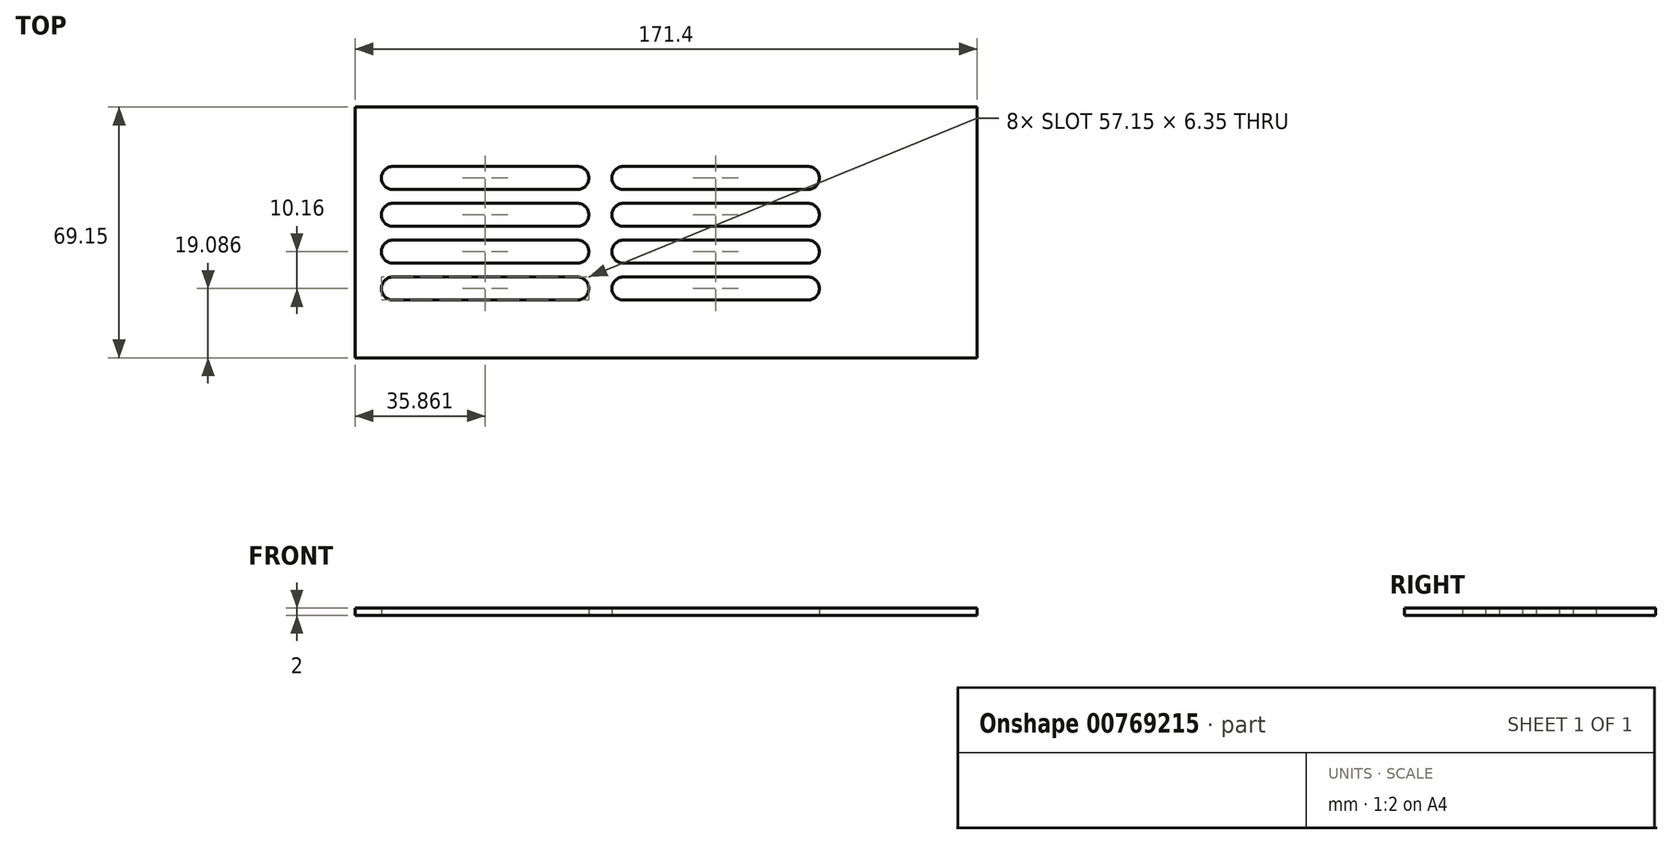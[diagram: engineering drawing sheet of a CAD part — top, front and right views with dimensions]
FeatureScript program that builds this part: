
annotation { "Feature Type Name" : "Feature", "Feature Type Description" : "" }
export const myFeature = defineFeature(function(context is Context, id is Id, definition is map)
    precondition{}
    {
        {
            var Q0;
            Q0=qCreatedBy(makeId("Top.planeOp"),FACE);
            var sketch = newSketch(context, id + "F0", { "sketchPlane" : qUnion([Q0])});
            skLineSegment(sketch, "E0.bottom", {"start": v(-93.16, 23.65) * mm, "end": v(-42.36, 23.65) * mm});
            skLineSegment(sketch, "E0.top", {"start": v(-93.16, 17.3) * mm, "end": v(-42.36, 17.3) * mm});
            skLineSegment(sketch, "E0.left", {"start": v(-96.33, 20.48) * mm, "end": v(-96.33, 20.48) * mm});
            skLineSegment(sketch, "E0.right", {"start": v(-39.18, 20.48) * mm, "end": v(-39.18, 20.48) * mm});
            skPoint(sketch, "E1.visualSharp", {"position": v(-96.33, 23.65) * mm});
            skArc(sketch, "E1.filletArc", {"start": v(-93.16, 23.65) * mm, "mid": v(-95.4, 22.72) * mm, "end": v(-96.33, 20.48) * mm});
            skPoint(sketch, "E2.visualSharp", {"position": v(-96.33, 17.3) * mm});
            skArc(sketch, "E2.filletArc", {"start": v(-96.33, 20.48) * mm, "mid": v(-95.4, 18.23) * mm, "end": v(-93.16, 17.3) * mm});
            skPoint(sketch, "E3.visualSharp", {"position": v(-39.18, 17.3) * mm});
            skArc(sketch, "E3.filletArc", {"start": v(-42.36, 17.3) * mm, "mid": v(-40.11, 18.23) * mm, "end": v(-39.18, 20.48) * mm});
            skPoint(sketch, "E4.visualSharp", {"position": v(-39.18, 23.65) * mm});
            skArc(sketch, "E4.filletArc", {"start": v(-39.18, 20.48) * mm, "mid": v(-40.11, 22.72) * mm, "end": v(-42.36, 23.65) * mm});
            skPoint(sketch, "E5.0.1.0", {"position": v(-39.18, 7.14) * mm});
            skLineSegment(sketch, "E5.0.1.1", {"start": v(-93.16, 7.14) * mm, "end": v(-42.36, 7.14) * mm});
            skPoint(sketch, "E5.0.1.2", {"position": v(-96.33, 13.5) * mm});
            skPoint(sketch, "E5.0.1.3", {"position": v(-39.18, 13.5) * mm});
            skPoint(sketch, "E5.0.1.4", {"position": v(-96.33, 7.14) * mm});
            skLineSegment(sketch, "E5.0.1.5", {"start": v(-93.16, 13.5) * mm, "end": v(-42.36, 13.5) * mm});
            skArc(sketch, "E5.0.1.6", {"start": v(-42.36, 7.14) * mm, "mid": v(-40.11, 8.07) * mm, "end": v(-39.18, 10.32) * mm});
            skArc(sketch, "E5.0.1.7", {"start": v(-96.33, 10.32) * mm, "mid": v(-95.4, 8.07) * mm, "end": v(-93.16, 7.14) * mm});
            skArc(sketch, "E5.0.1.8", {"start": v(-93.16, 13.5) * mm, "mid": v(-95.4, 12.56) * mm, "end": v(-96.33, 10.32) * mm});
            skArc(sketch, "E5.0.1.9", {"start": v(-39.18, 10.32) * mm, "mid": v(-40.11, 12.56) * mm, "end": v(-42.36, 13.5) * mm});
            skLineSegment(sketch, "E5.0.1.10", {"start": v(-96.33, 10.32) * mm, "end": v(-96.33, 10.32) * mm});
            skLineSegment(sketch, "E5.0.1.11", {"start": v(-39.18, 10.32) * mm, "end": v(-39.18, 10.32) * mm});
            skPoint(sketch, "E5.0.2.0", {"position": v(-39.18, -3.02) * mm});
            skLineSegment(sketch, "E5.0.2.1", {"start": v(-93.16, -3.02) * mm, "end": v(-42.36, -3.02) * mm});
            skPoint(sketch, "E5.0.2.2", {"position": v(-96.33, 3.33) * mm});
            skPoint(sketch, "E5.0.2.3", {"position": v(-39.18, 3.33) * mm});
            skPoint(sketch, "E5.0.2.4", {"position": v(-96.33, -3.02) * mm});
            skLineSegment(sketch, "E5.0.2.5", {"start": v(-93.16, 3.33) * mm, "end": v(-42.36, 3.33) * mm});
            skArc(sketch, "E5.0.2.6", {"start": v(-42.36, -3.02) * mm, "mid": v(-40.11, -2.09) * mm, "end": v(-39.18, 0.16) * mm});
            skArc(sketch, "E5.0.2.7", {"start": v(-96.33, 0.16) * mm, "mid": v(-95.4, -2.09) * mm, "end": v(-93.16, -3.02) * mm});
            skArc(sketch, "E5.0.2.8", {"start": v(-93.16, 3.33) * mm, "mid": v(-95.4, 2.4) * mm, "end": v(-96.33, 0.16) * mm});
            skArc(sketch, "E5.0.2.9", {"start": v(-39.18, 0.16) * mm, "mid": v(-40.11, 2.4) * mm, "end": v(-42.36, 3.33) * mm});
            skLineSegment(sketch, "E5.0.2.10", {"start": v(-96.33, 0.16) * mm, "end": v(-96.33, 0.16) * mm});
            skLineSegment(sketch, "E5.0.2.11", {"start": v(-39.18, 0.16) * mm, "end": v(-39.18, 0.16) * mm});
            skPoint(sketch, "E5.0.3.0", {"position": v(-39.18, -13.18) * mm});
            skLineSegment(sketch, "E5.0.3.1", {"start": v(-93.16, -13.18) * mm, "end": v(-42.36, -13.18) * mm});
            skPoint(sketch, "E5.0.3.2", {"position": v(-96.33, -6.83) * mm});
            skPoint(sketch, "E5.0.3.3", {"position": v(-39.18, -6.83) * mm});
            skPoint(sketch, "E5.0.3.4", {"position": v(-96.33, -13.18) * mm});
            skLineSegment(sketch, "E5.0.3.5", {"start": v(-93.16, -6.83) * mm, "end": v(-42.36, -6.83) * mm});
            skArc(sketch, "E5.0.3.6", {"start": v(-42.36, -13.18) * mm, "mid": v(-40.11, -12.25) * mm, "end": v(-39.18, -10) * mm});
            skArc(sketch, "E5.0.3.7", {"start": v(-96.33, -10) * mm, "mid": v(-95.4, -12.25) * mm, "end": v(-93.16, -13.18) * mm});
            skArc(sketch, "E5.0.3.8", {"start": v(-93.16, -6.83) * mm, "mid": v(-95.4, -7.76) * mm, "end": v(-96.33, -10) * mm});
            skArc(sketch, "E5.0.3.9", {"start": v(-39.18, -10) * mm, "mid": v(-40.11, -7.76) * mm, "end": v(-42.36, -6.83) * mm});
            skLineSegment(sketch, "E5.0.3.10", {"start": v(-96.33, -10) * mm, "end": v(-96.33, -10) * mm});
            skLineSegment(sketch, "E5.0.3.11", {"start": v(-39.18, -10) * mm, "end": v(-39.18, -10) * mm});
            skPoint(sketch, "E5.1.0.0", {"position": v(24.32, 17.3) * mm});
            skLineSegment(sketch, "E5.1.0.1", {"start": v(-29.66, 17.3) * mm, "end": v(21.14, 17.3) * mm});
            skPoint(sketch, "E5.1.0.2", {"position": v(-32.83, 23.65) * mm});
            skPoint(sketch, "E5.1.0.3", {"position": v(24.32, 23.65) * mm});
            skPoint(sketch, "E5.1.0.4", {"position": v(-32.83, 17.3) * mm});
            skLineSegment(sketch, "E5.1.0.5", {"start": v(-29.66, 23.65) * mm, "end": v(21.14, 23.65) * mm});
            skArc(sketch, "E5.1.0.6", {"start": v(21.14, 17.3) * mm, "mid": v(23.39, 18.23) * mm, "end": v(24.32, 20.48) * mm});
            skArc(sketch, "E5.1.0.7", {"start": v(-32.83, 20.48) * mm, "mid": v(-31.9, 18.23) * mm, "end": v(-29.66, 17.3) * mm});
            skArc(sketch, "E5.1.0.8", {"start": v(-29.66, 23.65) * mm, "mid": v(-31.9, 22.72) * mm, "end": v(-32.83, 20.48) * mm});
            skArc(sketch, "E5.1.0.9", {"start": v(24.32, 20.48) * mm, "mid": v(23.39, 22.72) * mm, "end": v(21.14, 23.65) * mm});
            skLineSegment(sketch, "E5.1.0.10", {"start": v(-32.83, 20.48) * mm, "end": v(-32.83, 20.48) * mm});
            skLineSegment(sketch, "E5.1.0.11", {"start": v(24.32, 20.48) * mm, "end": v(24.32, 20.48) * mm});
            skPoint(sketch, "E5.1.1.0", {"position": v(24.32, 7.14) * mm});
            skLineSegment(sketch, "E5.1.1.1", {"start": v(-29.66, 7.14) * mm, "end": v(21.14, 7.14) * mm});
            skPoint(sketch, "E5.1.1.2", {"position": v(-32.83, 13.5) * mm});
            skPoint(sketch, "E5.1.1.3", {"position": v(24.32, 13.5) * mm});
            skPoint(sketch, "E5.1.1.4", {"position": v(-32.83, 7.14) * mm});
            skLineSegment(sketch, "E5.1.1.5", {"start": v(-29.66, 13.5) * mm, "end": v(21.14, 13.5) * mm});
            skArc(sketch, "E5.1.1.6", {"start": v(21.14, 7.14) * mm, "mid": v(23.39, 8.07) * mm, "end": v(24.32, 10.32) * mm});
            skArc(sketch, "E5.1.1.7", {"start": v(-32.83, 10.32) * mm, "mid": v(-31.9, 8.07) * mm, "end": v(-29.66, 7.14) * mm});
            skArc(sketch, "E5.1.1.8", {"start": v(-29.66, 13.5) * mm, "mid": v(-31.9, 12.56) * mm, "end": v(-32.83, 10.32) * mm});
            skArc(sketch, "E5.1.1.9", {"start": v(24.32, 10.32) * mm, "mid": v(23.39, 12.56) * mm, "end": v(21.14, 13.5) * mm});
            skLineSegment(sketch, "E5.1.1.10", {"start": v(-32.83, 10.32) * mm, "end": v(-32.83, 10.32) * mm});
            skLineSegment(sketch, "E5.1.1.11", {"start": v(24.32, 10.32) * mm, "end": v(24.32, 10.32) * mm});
            skPoint(sketch, "E5.1.2.0", {"position": v(24.32, -3.02) * mm});
            skLineSegment(sketch, "E5.1.2.1", {"start": v(-29.66, -3.02) * mm, "end": v(21.14, -3.02) * mm});
            skPoint(sketch, "E5.1.2.2", {"position": v(-32.83, 3.33) * mm});
            skPoint(sketch, "E5.1.2.3", {"position": v(24.32, 3.33) * mm});
            skPoint(sketch, "E5.1.2.4", {"position": v(-32.83, -3.02) * mm});
            skLineSegment(sketch, "E5.1.2.5", {"start": v(-29.66, 3.33) * mm, "end": v(21.14, 3.33) * mm});
            skArc(sketch, "E5.1.2.6", {"start": v(21.14, -3.02) * mm, "mid": v(23.39, -2.09) * mm, "end": v(24.32, 0.16) * mm});
            skArc(sketch, "E5.1.2.7", {"start": v(-32.83, 0.16) * mm, "mid": v(-31.9, -2.09) * mm, "end": v(-29.66, -3.02) * mm});
            skArc(sketch, "E5.1.2.8", {"start": v(-29.66, 3.33) * mm, "mid": v(-31.9, 2.4) * mm, "end": v(-32.83, 0.16) * mm});
            skArc(sketch, "E5.1.2.9", {"start": v(24.32, 0.16) * mm, "mid": v(23.39, 2.4) * mm, "end": v(21.14, 3.33) * mm});
            skLineSegment(sketch, "E5.1.2.10", {"start": v(-32.83, 0.16) * mm, "end": v(-32.83, 0.16) * mm});
            skLineSegment(sketch, "E5.1.2.11", {"start": v(24.32, 0.16) * mm, "end": v(24.32, 0.16) * mm});
            skPoint(sketch, "E5.1.3.0", {"position": v(24.32, -13.18) * mm});
            skLineSegment(sketch, "E5.1.3.1", {"start": v(-29.66, -13.18) * mm, "end": v(21.14, -13.18) * mm});
            skPoint(sketch, "E5.1.3.2", {"position": v(-32.83, -6.83) * mm});
            skPoint(sketch, "E5.1.3.3", {"position": v(24.32, -6.83) * mm});
            skPoint(sketch, "E5.1.3.4", {"position": v(-32.83, -13.18) * mm});
            skLineSegment(sketch, "E5.1.3.5", {"start": v(-29.66, -6.83) * mm, "end": v(21.14, -6.83) * mm});
            skArc(sketch, "E5.1.3.6", {"start": v(21.14, -13.18) * mm, "mid": v(23.39, -12.25) * mm, "end": v(24.32, -10) * mm});
            skArc(sketch, "E5.1.3.7", {"start": v(-32.83, -10) * mm, "mid": v(-31.9, -12.25) * mm, "end": v(-29.66, -13.18) * mm});
            skArc(sketch, "E5.1.3.8", {"start": v(-29.66, -6.83) * mm, "mid": v(-31.9, -7.76) * mm, "end": v(-32.83, -10) * mm});
            skArc(sketch, "E5.1.3.9", {"start": v(24.32, -10) * mm, "mid": v(23.39, -7.76) * mm, "end": v(21.14, -6.83) * mm});
            skLineSegment(sketch, "E5.1.3.10", {"start": v(-32.83, -10) * mm, "end": v(-32.83, -10) * mm});
            skLineSegment(sketch, "E5.1.3.11", {"start": v(24.32, -10) * mm, "end": v(24.32, -10) * mm});
            skLineSegment(sketch, "E5.direction1", {"start": v(-96.33, 17.3) * mm, "end": v(-32.83, 17.3) * mm, "construction": true});
            skLineSegment(sketch, "E5.direction2", {"start": v(-96.33, 17.3) * mm, "end": v(-96.33, 7.14) * mm, "construction": true});
            skLineSegment(sketch, "E6.bottom", {"start": v(-103.62, 40.06) * mm, "end": v(67.78, 40.06) * mm});
            skLineSegment(sketch, "E6.top", {"start": v(-103.62, -29.1) * mm, "end": v(67.78, -29.1) * mm});
            skLineSegment(sketch, "E6.left", {"start": v(-103.62, 40.06) * mm, "end": v(-103.62, -29.1) * mm});
            skLineSegment(sketch, "E6.right", {"start": v(67.78, 40.06) * mm, "end": v(67.78, -29.1) * mm});
            skSolve(sketch);
        }
        {
            var Q0;
            Q0=makeQuery(id+"F0.imprint","IMPRINT",FACE,{"disambiguationData":[TD([[makeQuery(id+"F0.imprint","IMPRINT",EDGE,{"derivedFrom":sQuery(id+"F0.wireOp",EDGE,"E0.bottom")}),1.0]])]});
            extrude(context, id + "F1", {"entities" : qUnion([Q0]), "depth" : 2 * mm, "offsetDistance" : 25.4 * mm});
        }
    });
